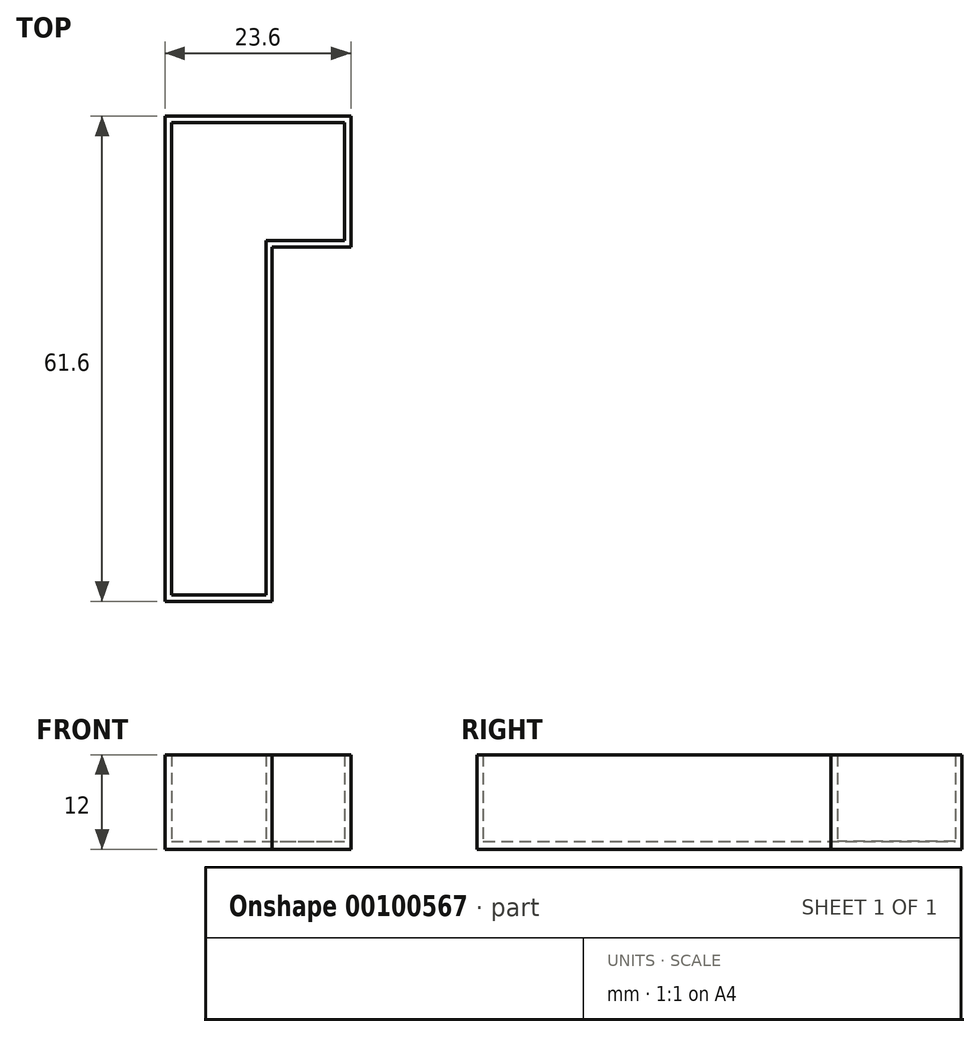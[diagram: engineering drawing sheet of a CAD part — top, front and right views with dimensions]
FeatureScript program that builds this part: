
annotation { "Feature Type Name" : "Feature", "Feature Type Description" : "" }
export const myFeature = defineFeature(function(context is Context, id is Id, definition is map)
    precondition{}
    {
        {
            var Q0;
            Q0=qCreatedBy(makeId("Top.planeOp"),FACE);
            var sketch = newSketch(context, id + "F0", { "sketchPlane" : qUnion([Q0])});
            skLineSegment(sketch, "E0.bottom", {"start": v(-6, -30) * mm, "end": v(6, -30) * mm});
            skLineSegment(sketch, "E0.top", {"start": v(-6, 30) * mm, "end": v(6, 30) * mm});
            skLineSegment(sketch, "E0.left", {"start": v(-6, -30) * mm, "end": v(-6, 30) * mm});
            skLineSegment(sketch, "E0.right", {"start": v(6, -30) * mm, "end": v(6, 15) * mm});
            skPoint(sketch, "E0.middle", {"position": v(0, 0) * mm});
            skLineSegment(sketch, "E1.bottom", {"start": v(6, 30) * mm, "end": v(16, 30) * mm});
            skLineSegment(sketch, "E1.top", {"start": v(6, 15) * mm, "end": v(16, 15) * mm});
            skLineSegment(sketch, "E1.right", {"start": v(16, 30) * mm, "end": v(16, 15) * mm});
            skLineSegment(sketch, "E2.bottom", {"start": v(6.8, -30.8) * mm, "end": v(-6.8, -30.8) * mm});
            skLineSegment(sketch, "E2.top", {"start": v(6.8, 30.8) * mm, "end": v(-6.8, 30.8) * mm});
            skLineSegment(sketch, "E2.left", {"start": v(6.8, -30.8) * mm, "end": v(6.8, 14.2) * mm});
            skLineSegment(sketch, "E2.right", {"start": v(-6.8, -30.8) * mm, "end": v(-6.8, 30.8) * mm});
            skLineSegment(sketch, "E3.bottom", {"start": v(6.8, 30.8) * mm, "end": v(16.8, 30.8) * mm});
            skLineSegment(sketch, "E3.top", {"start": v(6.8, 14.2) * mm, "end": v(16.8, 14.2) * mm});
            skLineSegment(sketch, "E3.right", {"start": v(16.8, 30.8) * mm, "end": v(16.8, 14.2) * mm});
            skSolve(sketch);
        }
        {
            var Q0;
            Q0=makeQuery(id+"F0.imprint","IMPRINT",FACE,{"disambiguationData":[TD([[makeQuery(id+"F0.imprint","IMPRINT",EDGE,{"derivedFrom":sQuery(id+"F0.wireOp",EDGE,"E0.bottom")}),-1.0]])]});
            extrude(context, id + "F1", {"entities" : qUnion([Q0]), "depth" : 12 * mm});
        }
        {
            var Q0;
            Q0=makeQuery(id+"F0.imprint","IMPRINT",FACE,{"disambiguationData":[TD([[makeQuery(id+"F0.imprint","IMPRINT",EDGE,{"derivedFrom":sQuery(id+"F0.wireOp",EDGE,"E0.bottom")}),1.0]])]});
            extrude(context, id + "F2", {"entities" : qUnion([Q0]), "operationType" : NewBodyOperationType.ADD, "depth" : 1 * mm});
        }
    });
